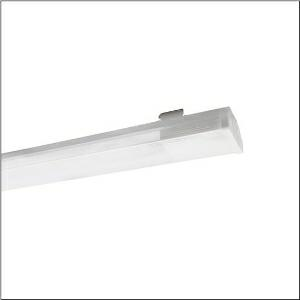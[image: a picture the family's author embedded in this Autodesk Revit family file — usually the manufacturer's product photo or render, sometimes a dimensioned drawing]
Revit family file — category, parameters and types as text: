
# Revit family: modario_r__31_gen_2_53bm8127u4gxc2_38ef
name_source: partatom
category: Lighting Fixtures
units: mm (PartAtom-declared; Revit-internal decimal feet)

## family parameters
Cut with Voids When Loaded = No
Host = Face
Light Source = No
Part Type = Normal
Room Calculation Point = No
Round Connector Dimension = Use Diameter
Shared = No

## types (1)
- Modario® 31 Gen.2 (1 x LED, 16360 lm, 90.4 W, 4000K)
    Apparent Load = 90 VA
    CIE Flux Codes = 47 80 95 93 100
    Color Rendering = 80
    Color Temperature = 4000K
    Default Elevation = 1800 mm
    Description = Modario® 31 Gen.2, luminaire insert, of sheet steel, coil coated, white, length: 2.392mm, width: 81mm, height: 82mm, 8x system unit, system units: 299mm, LED rated luminous flux: 16.360lm, light colour: 840, control gear: ON/OFF, with plug, 3-pole, with phase selection, mains connection: 220..240V, AC, 50/60Hz, rated input power: 90W, through-wiring accessed according to module size, primary optical cover: cover, of PMMA, light emission: direct distribution, primary light characteristic: symmetric, protection rating (complete): IP20, protection rating (LED compartment): IP50, insulation class (complete): insulation class I (protective earthing), certification: CE, ENEC, VDE, UKCA, impact resistance: IK03, permissible ambient temperature for indoor applications: -40..+40°C, corresponds to IFS (International Featured Standards) requirements for safety and quality in the food industry, reducing of maximum allowable ambient temperature of 5°C with ceiling mounting, packaging unit: 1 piece
    Height = 92 mm
    Lamp = 1 x LED
    Lamp Light Flux = 16360 lm
    Lamp Power = 90.4 W
    Lamp count = 1
    Length = 2392 mm
    Luminous efficacy = 181 lm/W
    Manufacturer = Siteco
    ModVariant = No
    Model = 53BM8127U4GXC2
    Mounting Place = Ceiling
    Mounting Type = Pendant
    Number of Poles = 1
    OnlyDefault = Yes
    Power Factor = 1
    Product Name = Modario® 31 Gen.2
    Product group = luminaire insert | ceiling pendant
    ProductGroupID = 902
    Protection Class = Protection class I
    Protection Degree = IP 20
    RLX_Detail_Level = 1
    RLX_Emergency_Light_Flux = 0 lm
    RLX_Emergency_Type = 0
    RLX_Emergency_Type_DB = No
    RlxData = <blob elided: 34645 chars, md5=7cff0067>
    Socket = socket
    Standby Power = 0 W
    System Light Flux = 16360 lm
    System Power = 90 W
    Type Comments = Product without accessories
    Type Image = l_1341883.jpg
    URL = http://relux.com
    VarID = ---
    Voltage = 0 V
    Weight = 0.00 kg
    Width = 81 mm

## geometry (parser evidence)
native form markers: Blend x4, Sweep x12
no freeform markers — native parametric forms only
